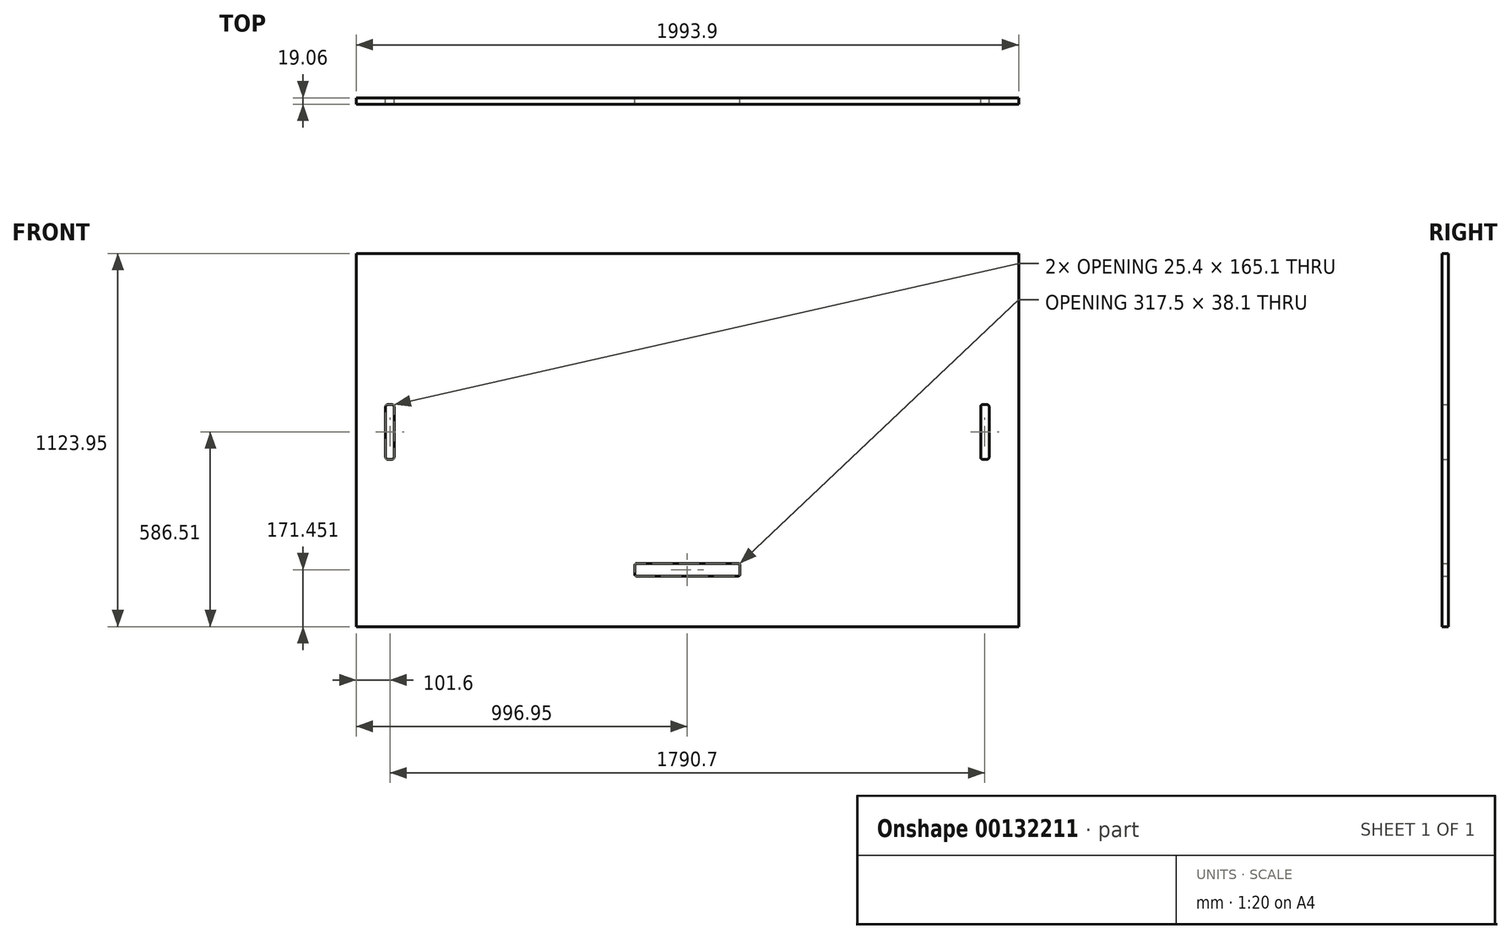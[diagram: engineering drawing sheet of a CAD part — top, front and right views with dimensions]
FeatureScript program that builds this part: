
annotation { "Feature Type Name" : "Feature", "Feature Type Description" : "" }
export const myFeature = defineFeature(function(context is Context, id is Id, definition is map)
    precondition{}
    {
        {
            var Q0;
            Q0=qCreatedBy(makeId("Front.planeOp"),FACE);
            var sketch = newSketch(context, id + "F0", { "sketchPlane" : qUnion([Q0])});
            skLineSegment(sketch, "E0.bottom", {"start": v(-996.95, -586.5) * mm, "end": v(996.95, -586.5) * mm});
            skLineSegment(sketch, "E0.top", {"start": v(-996.95, 537.44) * mm, "end": v(996.95, 537.44) * mm});
            skLineSegment(sketch, "E0.left", {"start": v(-996.95, -586.5) * mm, "end": v(-996.95, 537.44) * mm});
            skLineSegment(sketch, "E0.right", {"start": v(996.95, -586.5) * mm, "end": v(996.95, 537.44) * mm});
            skPoint(sketch, "E0.middle", {"position": v(0, -24.53) * mm});
            skLineSegment(sketch, "E1.bottom", {"start": v(889, -82.55) * mm, "end": v(901.7, -82.55) * mm});
            skLineSegment(sketch, "E1.top", {"start": v(889, 82.55) * mm, "end": v(901.7, 82.55) * mm});
            skLineSegment(sketch, "E1.left", {"start": v(882.65, -76.2) * mm, "end": v(882.65, 76.2) * mm});
            skLineSegment(sketch, "E1.right", {"start": v(908.05, -76.2) * mm, "end": v(908.05, 76.2) * mm});
            skPoint(sketch, "E1.middle", {"position": v(895.35, 0) * mm});
            skLineSegment(sketch, "E2.bottom", {"start": v(-889, -82.55) * mm, "end": v(-901.7, -82.55) * mm});
            skLineSegment(sketch, "E2.top", {"start": v(-889, 82.55) * mm, "end": v(-901.7, 82.55) * mm});
            skLineSegment(sketch, "E2.left", {"start": v(-882.65, -76.2) * mm, "end": v(-882.65, 76.2) * mm});
            skLineSegment(sketch, "E2.right", {"start": v(-908.05, -76.2) * mm, "end": v(-908.05, 76.2) * mm});
            skPoint(sketch, "E2.middle", {"position": v(-895.35, 0) * mm});
            skPoint(sketch, "E3.visualSharp", {"position": v(908.05, 82.55) * mm});
            skArc(sketch, "E3.filletArc", {"start": v(908.05, 76.2) * mm, "mid": v(906.2, 80.7) * mm, "end": v(901.7, 82.55) * mm});
            skPoint(sketch, "E4.visualSharp", {"position": v(882.65, -82.55) * mm});
            skArc(sketch, "E4.filletArc", {"start": v(882.65, -76.2) * mm, "mid": v(884.5, -80.7) * mm, "end": v(889, -82.55) * mm});
            skPoint(sketch, "E5.visualSharp", {"position": v(908.05, -82.55) * mm});
            skArc(sketch, "E5.filletArc", {"start": v(901.7, -82.55) * mm, "mid": v(906.2, -80.7) * mm, "end": v(908.05, -76.2) * mm});
            skPoint(sketch, "E6.visualSharp", {"position": v(882.65, 82.55) * mm});
            skArc(sketch, "E6.filletArc", {"start": v(889, 82.55) * mm, "mid": v(884.5, 80.7) * mm, "end": v(882.65, 76.2) * mm});
            skPoint(sketch, "E7.visualSharp", {"position": v(-908.05, 82.55) * mm});
            skArc(sketch, "E7.filletArc", {"start": v(-901.7, 82.55) * mm, "mid": v(-906.2, 80.7) * mm, "end": v(-908.05, 76.2) * mm});
            skPoint(sketch, "E8.visualSharp", {"position": v(-882.65, 82.55) * mm});
            skArc(sketch, "E8.filletArc", {"start": v(-882.65, 76.2) * mm, "mid": v(-884.5, 80.7) * mm, "end": v(-889, 82.55) * mm});
            skPoint(sketch, "E9.visualSharp", {"position": v(-882.65, -82.55) * mm});
            skArc(sketch, "E9.filletArc", {"start": v(-889, -82.55) * mm, "mid": v(-884.5, -80.7) * mm, "end": v(-882.65, -76.2) * mm});
            skPoint(sketch, "E10.visualSharp", {"position": v(-908.05, -82.55) * mm});
            skArc(sketch, "E10.filletArc", {"start": v(-908.05, -76.2) * mm, "mid": v(-906.2, -80.7) * mm, "end": v(-901.7, -82.55) * mm});
            skLineSegment(sketch, "E11.bottom", {"start": v(152.4, -396) * mm, "end": v(-152.4, -396) * mm});
            skLineSegment(sketch, "E11.top", {"start": v(152.4, -434.1) * mm, "end": v(-152.4, -434.1) * mm});
            skLineSegment(sketch, "E11.left", {"start": v(158.75, -402.36) * mm, "end": v(158.75, -427.76) * mm});
            skLineSegment(sketch, "E11.right", {"start": v(-158.75, -402.36) * mm, "end": v(-158.75, -427.76) * mm});
            skPoint(sketch, "E11.middle", {"position": v(0, -415.06) * mm});
            skPoint(sketch, "E12.visualSharp", {"position": v(158.75, -396) * mm});
            skArc(sketch, "E12.filletArc", {"start": v(158.75, -402.36) * mm, "mid": v(156.9, -397.87) * mm, "end": v(152.4, -396) * mm});
            skPoint(sketch, "E13.visualSharp", {"position": v(158.75, -434.1) * mm});
            skArc(sketch, "E13.filletArc", {"start": v(152.4, -434.1) * mm, "mid": v(156.9, -432.25) * mm, "end": v(158.75, -427.76) * mm});
            skPoint(sketch, "E14.visualSharp", {"position": v(-158.75, -396) * mm});
            skArc(sketch, "E14.filletArc", {"start": v(-152.4, -396) * mm, "mid": v(-156.9, -397.87) * mm, "end": v(-158.75, -402.36) * mm});
            skPoint(sketch, "E15.visualSharp", {"position": v(-158.75, -434.1) * mm});
            skArc(sketch, "E15.filletArc", {"start": v(-158.75, -427.76) * mm, "mid": v(-156.9, -432.25) * mm, "end": v(-152.4, -434.1) * mm});
            skSolve(sketch);
        }
        {
            var Q0;
            Q0=makeQuery(id+"F0.imprint","IMPRINT",FACE,{"disambiguationData":[TD([[makeQuery(id+"F0.imprint","IMPRINT",EDGE,{"derivedFrom":sQuery(id+"F0.wireOp",EDGE,"E0.bottom")}),1.0]])]});
            extrude(context, id + "F1", {"entities" : qUnion([Q0]), "endBound" : BoundingType.SYMMETRIC, "depth" : 19.05 * mm});
        }
    });
